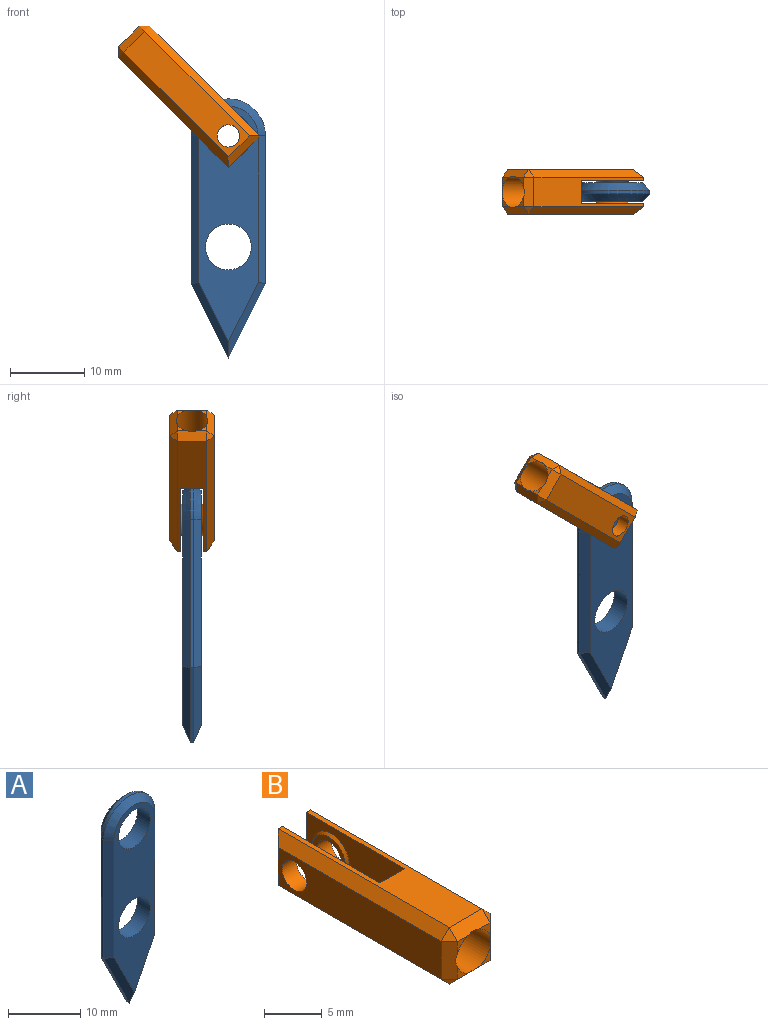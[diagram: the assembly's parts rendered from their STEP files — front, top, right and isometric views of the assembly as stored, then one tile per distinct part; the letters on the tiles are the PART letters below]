
ASSEMBLY  parts=2 mates=1
PART A: 19 faces, bbox 10x2.5x35 mm
  f0: plane 20x0.5mm, normal (-1,0,0), area 10mm2, adj f1,f8,f12,f16
  f1: plane 10x5mm, normal (-0.89,0,-0.45), area 5.6mm2, adj f0,f2,f10,f14
  f2: plane 10x5mm, normal (0.89,0,-0.45), area 5.6mm2, adj f1,f5,f9,f15
  f3: cylinder r=3.1mm len=6.2mm, axis (0,1,0), area 48.7mm2, adj f6,f7
  f4: cylinder r=3.1mm len=6.2mm, axis (0,1,0), area 48.7mm2, adj f6,f7
  f5: plane 20x0.5mm, normal (1,0,0), area 10mm2, adj f2,f8,f11,f17
  f6: plane 31.76x8mm, normal (0,-1,0), area 154.9mm2, adj f3,f4,f9,f10,f11,f12,f13
  f7: plane 31.76x8mm, normal (0,1,0), area 154.9mm2, adj f3,f4,f14,f15,f16,f17,f18
  f8: cylinder r=5mm len=10mm, axis (0,-1,0), area 7.9mm2, adj f0,f5,f13,f18
  f9: plane 10.24x5mm, normal (0.63,-0.71,-0.32), area 14.2mm2, adj f2,f6,f10,f11
  f10: plane 10.24x5mm, normal (-0.63,-0.71,-0.32), area 14.2mm2, adj f1,f6,f9,f12
  f11: plane 20x1mm, normal (0.71,-0.71,0), area 28.1mm2, adj f5,f6,f9,f13
  f12: plane 20x1mm, normal (-0.71,-0.71,0), area 28.1mm2, adj f0,f6,f10,f13
  f13: cone r=4mm half-angle=45deg, axis (0,1,0), area 20mm2, adj f6,f8,f11,f12
  f14: plane 10.24x5mm, normal (-0.63,0.71,-0.32), area 14.2mm2, adj f1,f7,f15,f16
  f15: plane 10.24x5mm, normal (0.63,0.71,-0.32), area 14.2mm2, adj f2,f7,f14,f17
  f16: plane 20x1mm, normal (-0.71,0.71,0), area 28.1mm2, adj f0,f7,f14,f18
  f17: plane 20x1mm, normal (0.71,0.71,0), area 28.1mm2, adj f5,f7,f15,f18
  f18: cone r=4mm half-angle=45deg, axis (0,-1,0), area 20mm2, adj f7,f8,f16,f17
PART B: 37 faces, bbox 6x22x6 mm
  f0: plane 1.36x1.36mm, normal (0,-1,0), area 0.6mm2, adj f11,f29,f34
  f1: plane 1.36x1.36mm, normal (0,-1,0), area 0.6mm2, adj f11,f30,f34
  f2: plane 1.36x1.36mm, normal (0,-1,0), area 0.6mm2, adj f11,f23,f30
  f3: plane 12x6mm, normal (1,0,0), area 48.1mm2, adj f4,f5,f8,f16,f20,f35,f36
  f4: plane 6x0.5mm, normal (0,1,0), area 3mm2, adj f3,f5,f8,f21
  f5: plane 21x4mm, normal (0,0,1), area 48mm2, adj f3,f4,f13,f15,f24,f30,f31,f36
  f6: cylinder r=1.5mm len=3mm, axis (-1,0,0), area 16.5mm2, adj f9,f17
  f7: plane 20x4mm, normal (-1,0,0), area 72.9mm2, adj f14,f21,f22,f23,f24
  f8: plane 21x4mm, normal (0,0,-1), area 48mm2, adj f3,f4,f13,f15,f22,f28,f29,f35
  f9: plane 20x4mm, normal (1,0,0), area 72.9mm2, adj f6,f27,f28,f31,f34
  f10: plane 1.36x1.36mm, normal (0,-1,0), area 0.6mm2, adj f11,f23,f29
  f11: cylinder r=2.1mm len=10mm, axis (0,-1,0), area 131.6mm2, adj f0,f1,f2,f10,f12,f23,f29,f30
  f12: plane 4.2x4.2mm, normal (0,-1,0), area 13.9mm2, adj f11
  f13: plane 6x0.5mm, normal (0,1,0), area 3mm2, adj f5,f8,f15,f27
  f14: cylinder r=1.5mm len=3mm, axis (-1,0,0), area 16.5mm2, adj f7,f18
  f15: plane 12x6mm, normal (-1,0,0), area 48.1mm2, adj f5,f8,f13,f16,f19,f35,f36
  f16: plane 3x2mm, normal (0,1,0), area 6mm2, adj f3,f15,f35,f36
  f17: plane 4x4mm, normal (-1,0,0), area 5.5mm2, adj f6,f19
  f18: plane 4x4mm, normal (1,0,0), area 5.5mm2, adj f14,f20
  f19: cone r=2mm half-angle=45deg, axis (1,0,0), area 4.7mm2, adj f15,f17
  f20: cone r=2mm half-angle=45deg, axis (-1,0,0), area 4.7mm2, adj f3,f18
  f21: plane 6x1mm, normal (-0.71,0.71,0), area 7.1mm2, adj f4,f7,f22,f24
  f22: plane 21x1mm, normal (-0.71,0,-0.71), area 29mm2, adj f7,f8,f21,f25
  f23: plane 4x1mm, normal (-0.71,-0.71,0), area 5.5mm2, adj f2,f7,f10,f11,f25,f26
  f24: plane 21x1mm, normal (-0.71,0,0.71), area 29mm2, adj f5,f7,f21,f26
  f25: plane 1x1mm, normal (-0.58,-0.58,-0.58), area 0.9mm2, adj f22,f23,f29
  f26: plane 1x1mm, normal (-0.58,-0.58,0.58), area 0.9mm2, adj f23,f24,f30
  f27: plane 6x1mm, normal (0.71,0.71,0), area 7.1mm2, adj f9,f13,f28,f31
  f28: plane 21x1mm, normal (0.71,0,-0.71), area 29mm2, adj f8,f9,f27,f32
  f29: plane 4x1mm, normal (0,-0.71,-0.71), area 5.5mm2, adj f0,f8,f10,f11,f25,f32
  f30: plane 4x1mm, normal (0,-0.71,0.71), area 5.5mm2, adj f1,f2,f5,f11,f26,f33
  f31: plane 21x1mm, normal (0.71,0,0.71), area 29mm2, adj f5,f9,f27,f33
  f32: plane 1x1mm, normal (0.58,-0.58,-0.58), area 0.9mm2, adj f28,f29,f34
  f33: plane 1x1mm, normal (0.58,-0.58,0.58), area 0.9mm2, adj f30,f31,f34
  f34: plane 4x1mm, normal (0.71,-0.71,0), area 5.5mm2, adj f0,f1,f9,f11,f32,f33
  f35: plane 3x2mm, normal (0,0.71,-0.71), area 8.5mm2, adj f3,f8,f15,f16
  f36: plane 3x2mm, normal (0,0.71,0.71), area 8.5mm2, adj f3,f5,f15,f16
PLACE A t=(13.07,-7.45,-17.04)mm
PLACE B rot(axis=(-0.68,-0.68,0.28),148.6deg) t=(10.25,20.86,5.03)mm
MATE revolute B.f6 <-> A.f4  axis (0,1,0) through (13.07,-8.7,-2.04)mm
